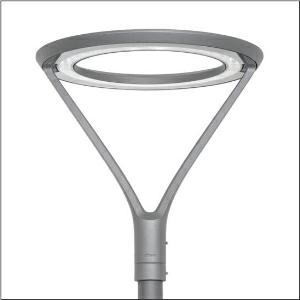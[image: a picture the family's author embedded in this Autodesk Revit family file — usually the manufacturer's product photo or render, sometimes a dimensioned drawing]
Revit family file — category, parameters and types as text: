
# Revit family: dl_r__20___pl1_2s_5xa51283ns008p_0781
name_source: partatom
category: Lighting Fixtures
units: mm (PartAtom-declared; Revit-internal decimal feet)

## family parameters
Cut with Voids When Loaded = No
Host = Face
Light Source = No
Part Type = Normal
Room Calculation Point = No
Round Connector Dimension = Use Diameter
Shared = No

## types (1)
- --- (1 x LED, 5400 lm, 41.9 W, 4000K)
    Apparent Load = 42 VA
    CIE Flux Codes = 33 78 99 100 100
    Color Rendering = 70
    Color Temperature = 4000K
    Default Elevation = 1800 mm
    Description = DL® 20, mast luminaire, primary light control with reflector, highly specular, primary optical cover: cover, of toughened safety glass of clear glass with excellent transmission level, light distribution: PL1.2s, light emission: direct distribution, primary light characteristic: symmetric, installation type: post-top, LED, High Power LED, rated luminous flux: 5.340lm, luminous efficacy: 101lm/W, light colour: 740, colour temperature: 4000K, control gear: ECG Plus, control: overheat protection, power reduction, digital communication interface, constant luminous flux control, time-dependent luminous flux control, flexible luminous flux parameterisation, electronic power reduction, mains connection: 230..240V, 50/60Hz, connection cable pre-assembled, cable length: 5m, start of lifetime: 53W, end of service life: 54W, reduction: 24W, luminaire housing, upper part, of cast aluminium, powder-coated, Siteco® metallic grey (DB 702S), diameter: 690mm, height: 690mm, spigot size: 76mm (post-top), luminaire housing, of cast aluminium, powder-coated, Siteco® metallic grey (DB 702S), equipment: Power, protection rating (complete): IP66, insulation class (complete): insulation class II (safety insulation), certification: CE, ENEC, VDE, impact resistance: IK08, permissible operating ambient temperature: -25..+30°C, standard-compliant lighting for roads and squares, packaging unit: 1 piece

Light Distribution: PL1.2s
    Height = 690 mm
    Lamp = 1 x LED
    Lamp Light Flux = 5400 lm
    Lamp Power = 41.9 W
    Lamp count = 1
    Length = 690 mm
    Luminous efficacy = 129 lm/W
    Manufacturer = Siteco
    ModVariant = No
    Model = 5XA51283NS008P
    Number of Poles = 1
    OnlyDefault = Yes
    Power Factor = 1
    Product Name = DL® 20 | PL1.2s
    Product group = mast luminaire | pylon top
    ProductGroupID = 6100
    Protection Class = Protection class II
    Protection Degree = IP 66
    RLX_Detail_Level = 1
    RLX_Emergency_Light_Flux = 0 lm
    RLX_Emergency_Type = 0
    RLX_Emergency_Type_DB = No
    RlxData = <blob elided: 205965 chars, md5=86f3b30c>
    Socket = socket
    Standby Power = 0 W
    System Light Flux = 5400 lm
    System Power = 42 W
    Type Comments = factory setting: luminous flux: 100 % | dim-lin: 254 | 565 mA
    Type Image = l_1006001.jpg
    URL = http://relux.com
    VarID = @adj_045879
    Voltage = 0 V
    Weight = 0.00 kg
    Width = 0 mm  [stored 0 ft]

note: [stored X ft] marks values corroborated as IEEE doubles in the binary element streams (Revit-internal decimal feet)

## geometry (parser evidence)
native form markers: Blend x4, Sweep x9
no freeform markers — native parametric forms only
